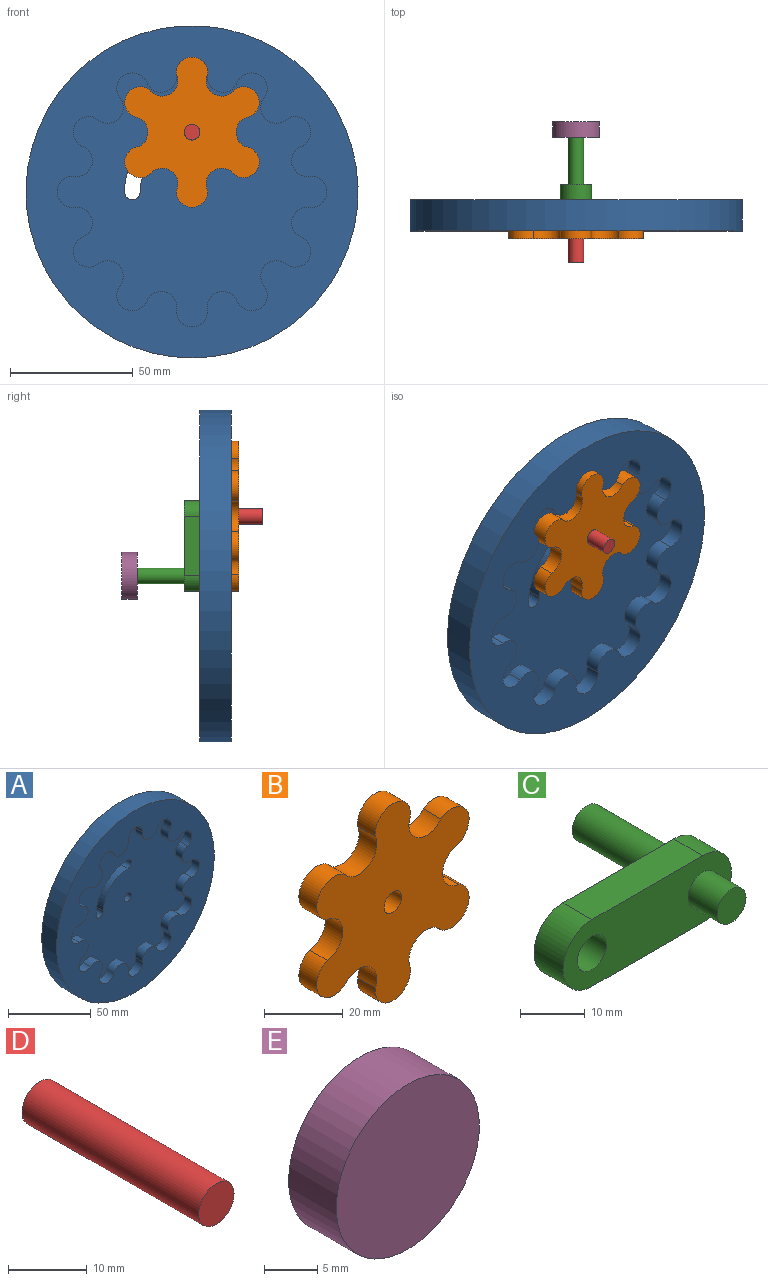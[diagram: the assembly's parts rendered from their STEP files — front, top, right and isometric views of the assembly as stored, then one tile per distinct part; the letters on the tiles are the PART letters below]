
ASSEMBLY  parts=5 mates=4
PART A: 33 faces, bbox 135.1x12.7x135.1 mm
  f0: cylinder r=27.43mm len=27.43mm, axis (0,1,0), area 273.6mm2, adj f1,f5,f6,f7
  f1: cylinder r=3.17mm len=6.35mm, axis (0,1,0), area 63.3mm2, adj f0,f2,f6,f7
  f2: cylinder r=21.08mm len=21.08mm, axis (0,1,0), area 210.3mm2, adj f1,f5,f6,f7
  f3: cylinder r=3.17mm len=6.35mm, axis (0,1,0), area 126.7mm2, adj f6,f7
  f4: cylinder r=67.56mm len=135.13mm, axis (0,1,0), area 5391.4mm2, adj f7,f32
  f5: cylinder r=3.17mm len=6.35mm, axis (0,1,0), area 63.3mm2, adj f0,f2,f6,f7
  f6: plane 109.73x109.73mm, normal (0,-1,0), area 7131mm2, adj f0,f1,f2,f3,f5,f8,f9,f10
  f7: plane 135.13x135.13mm, normal (0,1,0), area 14035.7mm2, adj f0,f1,f2,f3,f4,f5
  f8: cylinder r=6.35mm len=12.7mm, axis (0,1,0), area 131.2mm2, adj f6,f9,f31,f32
  f9: cylinder r=6.35mm len=12.38mm, axis (0,1,0), area 122.1mm2, adj f6,f8,f10,f32
  f10: cylinder r=6.35mm len=12.02mm, axis (0,1,0), area 131.2mm2, adj f6,f9,f11,f32
  f11: cylinder r=6.35mm len=10.58mm, axis (0,1,0), area 122.1mm2, adj f6,f10,f12,f32
  f12: cylinder r=6.35mm len=12.02mm, axis (0,1,0), area 131.2mm2, adj f6,f11,f13,f32
  f13: cylinder r=6.35mm len=12.38mm, axis (0,1,0), area 122.1mm2, adj f6,f12,f14,f32
  f14: cylinder r=6.35mm len=12.7mm, axis (0,1,0), area 131.2mm2, adj f6,f13,f15,f32
  f15: cylinder r=6.35mm len=12.38mm, axis (0,1,0), area 122.1mm2, adj f6,f14,f16,f32
  f16: cylinder r=6.35mm len=12.02mm, axis (0,1,0), area 131.2mm2, adj f6,f15,f17,f32
  f17: cylinder r=6.35mm len=10.58mm, axis (0,1,0), area 122.1mm2, adj f6,f16,f18,f32
  f18: cylinder r=6.35mm len=12.02mm, axis (0,1,0), area 131.2mm2, adj f6,f17,f19,f32
  f19: cylinder r=6.35mm len=12.38mm, axis (0,1,0), area 122.1mm2, adj f6,f18,f20,f32
  f20: cylinder r=6.35mm len=12.7mm, axis (0,1,0), area 131.2mm2, adj f6,f19,f21,f32
  f21: cylinder r=6.35mm len=12.38mm, axis (0,1,0), area 122.1mm2, adj f6,f20,f22,f32
  f22: cylinder r=6.35mm len=12.02mm, axis (0,1,0), area 131.2mm2, adj f6,f21,f23,f32
  f23: cylinder r=6.35mm len=10.58mm, axis (0,1,0), area 122.1mm2, adj f6,f22,f24,f32
  f24: cylinder r=6.35mm len=12.02mm, axis (0,1,0), area 131.2mm2, adj f6,f23,f25,f32
  f25: cylinder r=6.35mm len=12.38mm, axis (0,1,0), area 122.1mm2, adj f6,f24,f26,f32
  f26: cylinder r=6.35mm len=12.7mm, axis (0,1,0), area 131.2mm2, adj f6,f25,f27,f32
  f27: cylinder r=6.35mm len=12.38mm, axis (0,1,0), area 122.1mm2, adj f6,f26,f28,f32
  f28: cylinder r=6.35mm len=12.02mm, axis (0,1,0), area 131.2mm2, adj f6,f27,f29,f32
  f29: cylinder r=6.35mm len=10.58mm, axis (0,1,0), area 122.1mm2, adj f6,f28,f30,f32
  f30: cylinder r=6.35mm len=12.02mm, axis (0,1,0), area 131.2mm2, adj f6,f29,f31,f32
  f31: cylinder r=6.35mm len=12.38mm, axis (0,1,0), area 122.1mm2, adj f6,f8,f30,f32
  f32: plane 135.13x135.13mm, normal (0,-1,0), area 6904.7mm2, adj f4,f8,f9,f10,f11,f12,f13,f14
PART B: 15 faces, bbox 54.7x6.4x61.2 mm
  f0: cylinder r=6.35mm len=11.46mm, axis (0,1,0), area 117.7mm2, adj f1,f12,f13,f14
  f1: cylinder r=6.35mm len=12.7mm, axis (0,1,0), area 135.6mm2, adj f0,f2,f13,f14
  f2: cylinder r=6.35mm len=11.46mm, axis (0,1,0), area 117.7mm2, adj f1,f3,f13,f14
  f3: cylinder r=6.35mm len=12.17mm, axis (0,1,0), area 135.6mm2, adj f2,f4,f13,f14
  f4: cylinder r=6.35mm len=12.62mm, axis (0,1,0), area 117.7mm2, adj f3,f5,f13,f14
  f5: cylinder r=6.35mm len=12.17mm, axis (0,1,0), area 135.6mm2, adj f4,f6,f13,f14
  f6: cylinder r=6.35mm len=11.46mm, axis (0,1,0), area 117.7mm2, adj f5,f7,f13,f14
  f7: cylinder r=6.35mm len=12.7mm, axis (0,1,0), area 135.6mm2, adj f6,f8,f13,f14
  f8: cylinder r=6.35mm len=11.46mm, axis (0,1,0), area 117.7mm2, adj f7,f9,f13,f14
  f9: cylinder r=6.35mm len=12.17mm, axis (0,1,0), area 135.6mm2, adj f8,f10,f13,f14
  f10: cylinder r=6.35mm len=12.62mm, axis (0,1,0), area 117.7mm2, adj f9,f12,f13,f14
  f11: cylinder r=3.17mm len=6.35mm, axis (0,1,0), area 126.7mm2, adj f13,f14
  f12: cylinder r=6.35mm len=12.17mm, axis (0,1,0), area 135.6mm2, adj f0,f10,f13,f14
  f13: plane 61.21x54.71mm, normal (0,-1,0), area 1859.1mm2, adj f0,f1,f2,f3,f4,f5,f6,f7
  f14: plane 61.21x54.71mm, normal (0,1,0), area 1859.1mm2, adj f0,f1,f2,f3,f4,f5,f6,f7
PART C: 11 faces, bbox 37x31.8x12.7 mm
  f0: cylinder r=6.35mm len=12.7mm, axis (0,-1,0), area 126.7mm2, adj f1,f4,f5,f6
  f1: plane 24.26x6.35mm, normal (0,0,1), area 154mm2, adj f0,f2,f5,f6
  f2: cylinder r=6.35mm len=12.7mm, axis (0,-1,0), area 126.7mm2, adj f1,f4,f5,f6
  f3: cylinder r=3.17mm len=6.35mm, axis (0,-1,0), area 126.7mm2, adj f5,f6
  f4: plane 24.26x6.35mm, normal (0,0,-1), area 154mm2, adj f0,f2,f5,f6
  f5: plane 36.96x12.7mm, normal (0,1,0), area 371.4mm2, adj f0,f1,f2,f3,f4,f9
  f6: plane 36.96x12.7mm, normal (0,-1,0), area 371.4mm2, adj f0,f1,f2,f3,f4,f8
  f7: plane 6.35x6.35mm, normal (0,-1,0), area 31.7mm2, adj f8
  f8: cylinder r=3.17mm len=6.35mm, axis (0,1,0), area 126.7mm2, adj f6,f7
  f9: cylinder r=3.17mm len=19.05mm, axis (0,1,0), area 380mm2, adj f5,f10
  f10: plane 6.35x6.35mm, normal (0,1,0), area 31.7mm2, adj f9
PART D: 3 faces, bbox 6.4x31.8x6.4 mm
  f0: cylinder r=3.17mm len=31.75mm, axis (0,1,0), area 633.4mm2, adj f1,f2
  f1: plane 6.35x6.35mm, normal (0,-1,0), area 31.7mm2, adj f0
  f2: plane 6.35x6.35mm, normal (0,1,0), area 31.7mm2, adj f0
PART E: 3 faces, bbox 19.1x6.4x19.1 mm
  f0: cylinder r=9.53mm len=19.05mm, axis (0,-1,0), area 380mm2, adj f1,f2
  f1: plane 19.05x19.05mm, normal (0,1,0), area 285mm2, adj f0
  f2: plane 19.05x19.05mm, normal (0,-1,0), area 285mm2, adj f0
PLACE A t=(0,-25.4,0)mm fixed
PLACE B rot(axis=(0,-1,0),180deg) t=(0,-34.92,24.26)mm
PLACE C rot(axis=(0,1,0),90deg) t=(0,-25.4,0)mm
PLACE D rot(axis=(0,1,0),90deg) t=(0,-25.4,0)mm
PLACE E at identity fixed
MATE fastened D.f0 <-> C.f3  axis (0,1,0) through (0,-19.05,24.26)mm
MATE revolute A.f4 <-> C.f8  axis (0,1,0) through (0,-25.4,0)mm
MATE revolute B.f11 <-> D.f0  axis (0,1,0) through (0,-34.92,24.26)mm
MATE revolute C.f8 <-> E.f0  axis (0,1,0) through (0,0,0)mm
